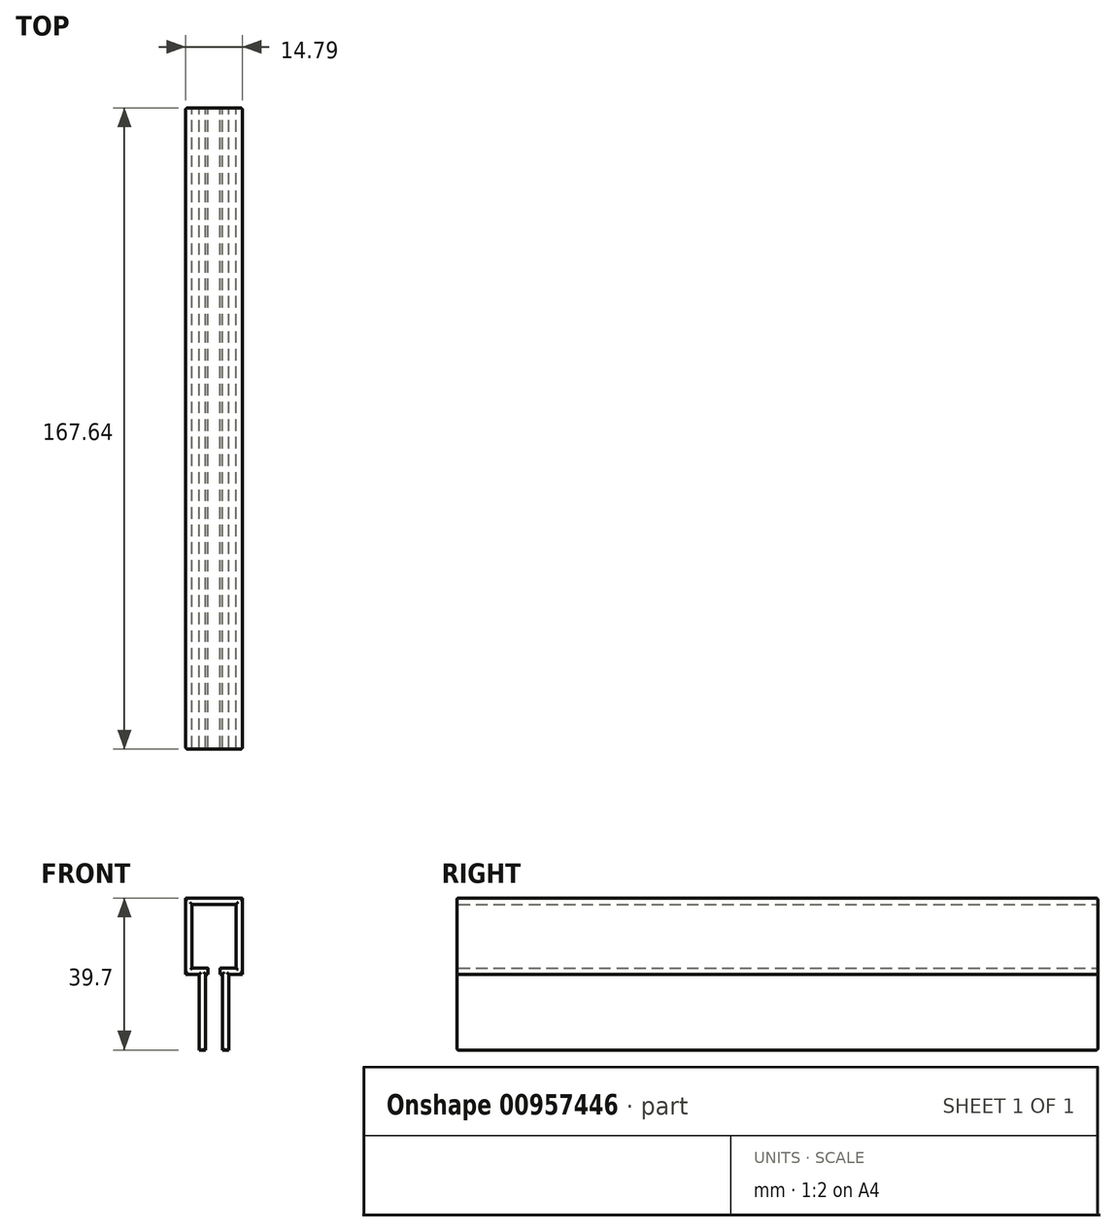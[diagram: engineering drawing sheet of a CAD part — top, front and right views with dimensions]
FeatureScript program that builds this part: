
annotation { "Feature Type Name" : "Feature", "Feature Type Description" : "" }
export const myFeature = defineFeature(function(context is Context, id is Id, definition is map)
    precondition{}
    {
        {
            var Q0;
            Q0=qCreatedBy(makeId("Front.planeOp"),FACE);
            var sketch = newSketch(context, id + "F0", { "sketchPlane" : qUnion([Q0])});
            skLineSegment(sketch, "E0", {"start": v(-5.89, -1.71) * mm, "end": v(-5.89, 18.1) * mm});
            skLineSegment(sketch, "E1.MirrorCS", {"start": v(-5.25, 18.1) * mm, "end": v(-5.89, 18.1) * mm});
            skLineSegment(sketch, "E2.MirrorCS", {"start": v(-2.08, 19.7) * mm, "end": v(-2.08, 18.1) * mm});
            skLineSegment(sketch, "E3.MirrorCS", {"start": v(-2.08, 18.1) * mm, "end": v(-1.45, 18.1) * mm});
            skLineSegment(sketch, "E4", {"start": v(-5.89, -1.71) * mm, "end": v(-7.49, -1.71) * mm});
            skLineSegment(sketch, "E5", {"start": v(-1.45, -1.71) * mm, "end": v(-1.45, 18.1) * mm});
            skLineSegment(sketch, "E6", {"start": v(-7.49, -1.71) * mm, "end": v(-7.5, 18.1) * mm});
            skLineSegment(sketch, "E7", {"start": v(-5.25, 18.1) * mm, "end": v(-5.25, 19.7) * mm});
            skLineSegment(sketch, "E8", {"start": v(0.15, 18.1) * mm, "end": v(0.15, -1.71) * mm});
            skLineSegment(sketch, "E9", {"start": v(0.15, -1.71) * mm, "end": v(-1.45, -1.71) * mm});
            skLineSegment(sketch, "E10", {"start": v(2.13, 19.7) * mm, "end": v(2.13, 36.39) * mm});
            skLineSegment(sketch, "E11", {"start": v(-9.46, 19.7) * mm, "end": v(-9.46, 36.39) * mm});
            skLineSegment(sketch, "E12", {"start": v(-9.46, 36.39) * mm, "end": v(2.13, 36.39) * mm});
            skLineSegment(sketch, "E13", {"start": v(-5.25, 19.7) * mm, "end": v(-9.46, 19.7) * mm});
            skLineSegment(sketch, "E14", {"start": v(2.13, 19.7) * mm, "end": v(-2.08, 19.7) * mm});
            skLineSegment(sketch, "E15", {"start": v(0.15, 18.1) * mm, "end": v(3.73, 18.1) * mm});
            skLineSegment(sketch, "E16", {"start": v(3.73, 18.1) * mm, "end": v(3.73, 37.99) * mm});
            skLineSegment(sketch, "E17.MirrorCS", {"start": v(-11.06, 18.1) * mm, "end": v(-11.06, 37.99) * mm});
            skLineSegment(sketch, "E18.MirrorCS", {"start": v(-7.49, 18.1) * mm, "end": v(-11.06, 18.1) * mm});
            skLineSegment(sketch, "E19", {"start": v(3.73, 37.99) * mm, "end": v(-11.06, 37.99) * mm});
            skSolve(sketch);
        }
        {
            var Q0;
            Q0=makeQuery(id+"F0.imprint","IMPRINT",FACE,{"disambiguationData":[TD([[makeQuery(id+"F0.imprint","IMPRINT",EDGE,{"derivedFrom":sQuery(id+"F0.wireOp",EDGE,"E0")}),1.0]])]});
            extrude(context, id + "F1", {"entities" : qUnion([Q0]), "depth" : 167.64 * mm, "offsetDistance" : 25.4 * mm});
        }
        {
            var Q0;
            Q0=makeQuery(id+"F1.opExtrude","CAP_FACE",FACE,{"disambiguationData":[OSD([sQuery(id+"F0.wireOp",EDGE,"E0"),sQuery(id+"F0.wireOp",EDGE,"E1.MirrorCS"),sQuery(id+"F0.wireOp",EDGE,"E2.MirrorCS"),sQuery(id+"F0.wireOp",EDGE,"E3.MirrorCS"),sQuery(id+"F0.wireOp",EDGE,"E4"),sQuery(id+"F0.wireOp",EDGE,"E5"),sQuery(id+"F0.wireOp",EDGE,"E6"),sQuery(id+"F0.wireOp",EDGE,"E7"),sQuery(id+"F0.wireOp",EDGE,"E8"),sQuery(id+"F0.wireOp",EDGE,"E9"),sQuery(id+"F0.wireOp",EDGE,"E10"),sQuery(id+"F0.wireOp",EDGE,"E11"),sQuery(id+"F0.wireOp",EDGE,"E12"),sQuery(id+"F0.wireOp",EDGE,"E13"),sQuery(id+"F0.wireOp",EDGE,"E14"),sQuery(id+"F0.wireOp",EDGE,"E15"),sQuery(id+"F0.wireOp",EDGE,"E16"),sQuery(id+"F0.wireOp",EDGE,"E17.MirrorCS"),sQuery(id+"F0.wireOp",EDGE,"E18.MirrorCS"),sQuery(id+"F0.wireOp",EDGE,"E19")])],"isStart":true});
            var Q1;
            Q1=makeQuery(id+"F1.opExtrude","CAP_FACE",FACE,{"disambiguationData":[OSD([sQuery(id+"F0.wireOp",EDGE,"E0"),sQuery(id+"F0.wireOp",EDGE,"E1.MirrorCS"),sQuery(id+"F0.wireOp",EDGE,"E2.MirrorCS"),sQuery(id+"F0.wireOp",EDGE,"E3.MirrorCS"),sQuery(id+"F0.wireOp",EDGE,"E4"),sQuery(id+"F0.wireOp",EDGE,"E5"),sQuery(id+"F0.wireOp",EDGE,"E6"),sQuery(id+"F0.wireOp",EDGE,"E7"),sQuery(id+"F0.wireOp",EDGE,"E8"),sQuery(id+"F0.wireOp",EDGE,"E9"),sQuery(id+"F0.wireOp",EDGE,"E10"),sQuery(id+"F0.wireOp",EDGE,"E11"),sQuery(id+"F0.wireOp",EDGE,"E12"),sQuery(id+"F0.wireOp",EDGE,"E13"),sQuery(id+"F0.wireOp",EDGE,"E14"),sQuery(id+"F0.wireOp",EDGE,"E15"),sQuery(id+"F0.wireOp",EDGE,"E16"),sQuery(id+"F0.wireOp",EDGE,"E17.MirrorCS"),sQuery(id+"F0.wireOp",EDGE,"E18.MirrorCS"),sQuery(id+"F0.wireOp",EDGE,"E19")])],"isStart":false});
            fillet(context, id + "F2", {"entities" : qUnion([Q0, Q1]), "radius" : 0.43 * mm, "tangentPropagation" : true, "allowEdgeOverflow" : false});
        }
    });
